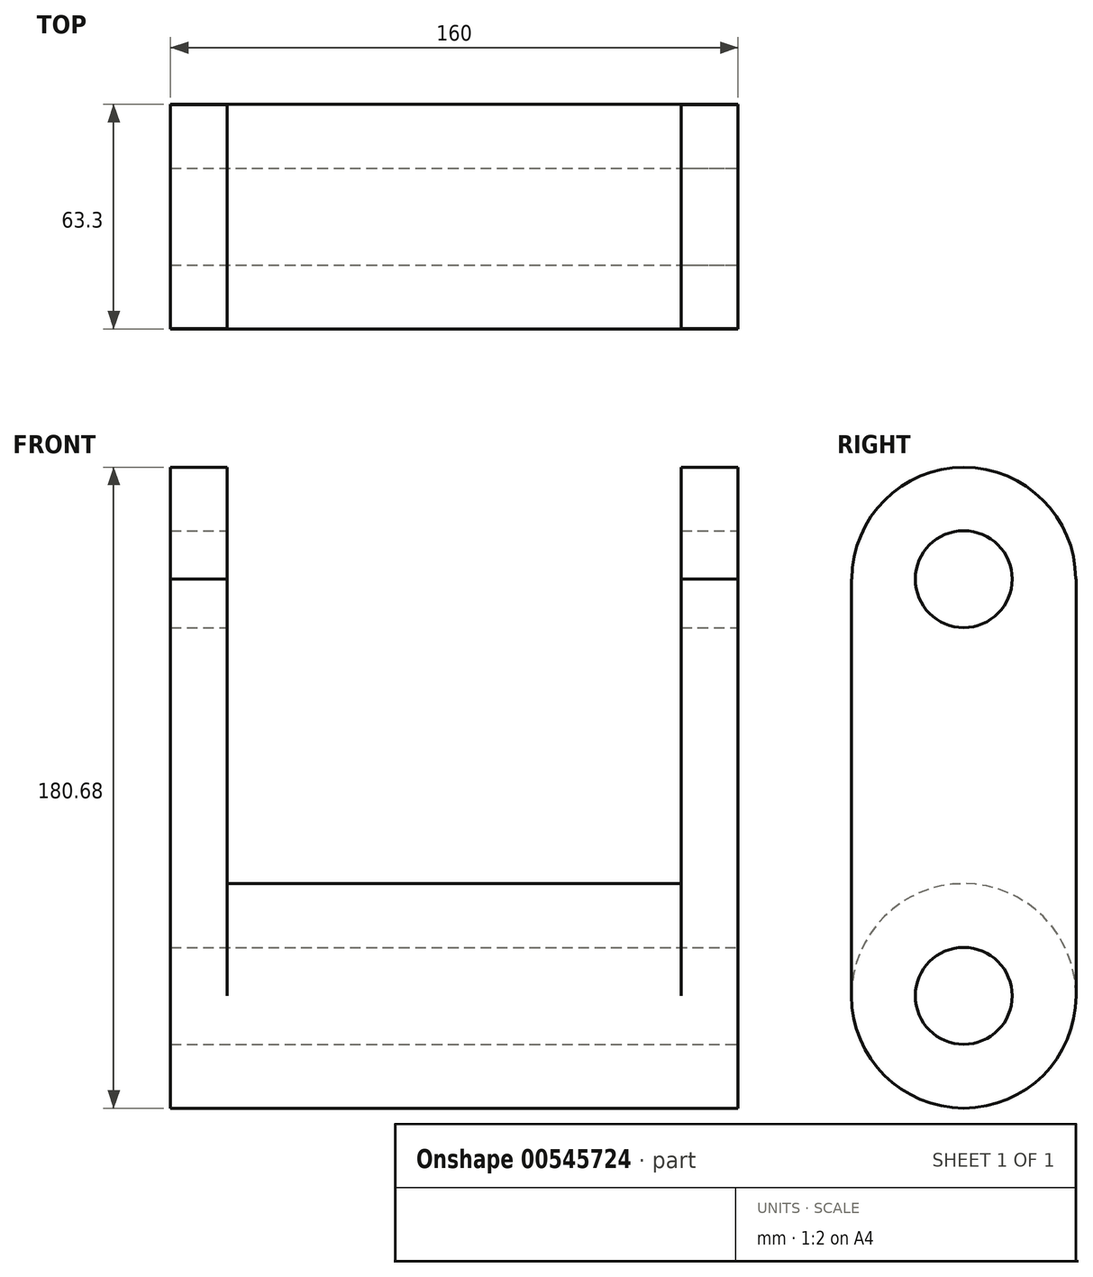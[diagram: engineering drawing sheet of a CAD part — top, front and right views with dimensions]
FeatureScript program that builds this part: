
annotation { "Feature Type Name" : "Feature", "Feature Type Description" : "" }
export const myFeature = defineFeature(function(context is Context, id is Id, definition is map)
    precondition{}
    {
        {
            var Q0;
            Q0=qCreatedBy(makeId("Right.planeOp"),FACE);
            var sketch = newSketch(context, id + "F0", { "sketchPlane" : qUnion([Q0])});
            skCircle(sketch, "E0", {"center": v(0, 0) * mm, "radius": 31.65 * mm});
            skSolve(sketch);
        }
        {
            var Q0;
            Q0 = qSketchRegion(id + "F0", true);
            extrude(context, id + "F1", {"entities" : qUnion([Q0]), "depth" : 80 * mm, "offsetDistance" : 25 * mm});
        }
        {
            var Q0;
            Q0=makeQuery(id+"F1.opExtrude","CAP_FACE",FACE,{"disambiguationData":[OSD([sQuery(id+"F0.wireOp",EDGE,"E0")])],"isStart":false});
            var sketch = newSketch(context, id + "F2", { "sketchPlane" : qUnion([Q0])});
            skPoint(sketch, "E1.end.orphan", {"position": v(-31.65, 117.5) * mm});
            skPoint(sketch, "E1.start.orphan", {"position": v(-31.65, 0) * mm});
            skPoint(sketch, "E2.end.orphan", {"position": v(31.65, 117.5) * mm});
            skPoint(sketch, "E2.start.orphan", {"position": v(31.65, 0) * mm});
            skLineSegment(sketch, "E3.bottom", {"start": v(31.65, 117.5) * mm, "end": v(-31.65, 117.5) * mm});
            skLineSegment(sketch, "E3.left", {"start": v(31.65, 117.5) * mm, "end": v(31.65, 0) * mm});
            skLineSegment(sketch, "E3.right", {"start": v(-31.65, 117.5) * mm, "end": v(-31.65, 0) * mm});
            skPoint(sketch, "E3.middle", {"position": v(0, 0) * mm});
            skPoint(sketch, "E4.middle", {"position": v(-39.72, -36.46) * mm});
            skPoint(sketch, "E4.top.end.orphan", {"position": v(-47.8, -32.34) * mm});
            skPoint(sketch, "E4.bottom.end.orphan", {"position": v(-47.8, -40.58) * mm});
            skPoint(sketch, "E5.trimOffspring.start.orphan", {"position": v(-31.65, -40.58) * mm});
            skPoint(sketch, "E6.orphan", {"position": v(-31.65, -32.34) * mm});
            skPoint(sketch, "E3.top.end.orphan", {"position": v(-31.65, -117.5) * mm});
            skPoint(sketch, "E3.top.start.orphan", {"position": v(31.65, -117.5) * mm});
            skLineSegment(sketch, "E7", {"start": v(-31.65, 0) * mm, "end": v(31.65, 0) * mm});
            skArc(sketch, "E8", {"start": v(31.65, 0) * mm, "mid": v(0, 31.65) * mm, "end": v(-31.65, 0) * mm});
            skArc(sketch, "E9", {"start": v(-31.65, 0) * mm, "mid": v(0, -31.65) * mm, "end": v(31.65, 0) * mm});
            skSolve(sketch);
        }
        {
            var Q0;
            Q0 = qSketchRegion(id + "F2", true);
            extrude(context, id + "F3", {"entities" : qUnion([Q0]), "operationType" : NewBodyOperationType.ADD, "oppositeDirection" : true, "depth" : 16 * mm, "offsetDistance" : 25 * mm});
        }
        {
            var Q0;
            Q0=makeQuery(id+"F3.boolean.opBoolean","MERGE",FACE,{"derivedFrom":[makeQuery(id+"F1.opExtrude","CAP_FACE",FACE,{"disambiguationData":[OSD([sQuery(id+"F0.wireOp",EDGE,"E0")])],"isStart":false}),makeQuery(id+"F3.opExtrude","CAP_FACE",FACE,{"disambiguationData":[OSD([sQuery(id+"F2.wireOp",EDGE,"E3.bottom"),sQuery(id+"F2.wireOp",EDGE,"E3.left"),sQuery(id+"F2.wireOp",EDGE,"E3.right"),sQuery(id+"F2.wireOp",EDGE,"E9")])],"isStart":true})]});
            var sketch = newSketch(context, id + "F4", { "sketchPlane" : qUnion([Q0])});
            skCircle(sketch, "E10", {"center": v(0, 117.5) * mm, "radius": 31.53 * mm});
            skSolve(sketch);
        }
        {
            var Q0;
            Q0 = qSketchRegion(id + "F4", true);
            extrude(context, id + "F5", {"entities" : qUnion([Q0]), "operationType" : NewBodyOperationType.ADD, "oppositeDirection" : true, "depth" : 16 * mm, "offsetDistance" : 25 * mm});
        }
        {
            var Q0;
            Q0=makeQuery(id+"F1.opExtrude","SWEPT_BODY",BODY,{"disambiguationData":[OSD([sQuery(id+"F0.wireOp",EDGE,"E0")])]});
            var Q1;
            Q1=makeQuery(id+"F1.opExtrude","CAP_FACE",FACE,{"disambiguationData":[OSD([sQuery(id+"F0.wireOp",EDGE,"E0")])],"isStart":true});
            mirror(context, id + "F6", {"operationType" : NewBodyOperationType.ADD, "entities" : qUnion([Q0]), "mirrorPlane" : qUnion([Q1])});
        }
        {
            var Q0;
            Q0=makeQuery(id+"F5.boolean.opBoolean","MERGE",FACE,{"derivedFrom":[makeQuery(id+"F3.boolean.opBoolean","MERGE",FACE,{"derivedFrom":[makeQuery(id+"F1.opExtrude","CAP_FACE",FACE,{"disambiguationData":[OSD([sQuery(id+"F0.wireOp",EDGE,"E0")])],"isStart":false}),makeQuery(id+"F3.opExtrude","CAP_FACE",FACE,{"disambiguationData":[OSD([sQuery(id+"F2.wireOp",EDGE,"E3.bottom"),sQuery(id+"F2.wireOp",EDGE,"E3.left"),sQuery(id+"F2.wireOp",EDGE,"E3.right"),sQuery(id+"F2.wireOp",EDGE,"E9")])],"isStart":true})]}),makeQuery(id+"F5.opExtrude","CAP_FACE",FACE,{"disambiguationData":[OSD([sQuery(id+"F4.wireOp",EDGE,"E10")])],"isStart":true})]});
            var sketch = newSketch(context, id + "F7", { "sketchPlane" : qUnion([Q0])});
            skCircle(sketch, "E11", {"center": v(0, 0) * mm, "radius": 13.66 * mm});
            skSolve(sketch);
        }
        {
            var Q0;
            Q0 = qSketchRegion(id + "F7", true);
            extrude(context, id + "F8", {"entities" : qUnion([Q0]), "operationType" : NewBodyOperationType.REMOVE, "oppositeDirection" : true, "depth" : 193 * mm, "offsetDistance" : 25 * mm});
        }
        {
            var Q0;
            Q0=makeQuery(id+"F5.boolean.opBoolean","MERGE",FACE,{"derivedFrom":[makeQuery(id+"F3.boolean.opBoolean","MERGE",FACE,{"derivedFrom":[makeQuery(id+"F1.opExtrude","CAP_FACE",FACE,{"disambiguationData":[OSD([sQuery(id+"F0.wireOp",EDGE,"E0")])],"isStart":false}),makeQuery(id+"F3.opExtrude","CAP_FACE",FACE,{"disambiguationData":[OSD([sQuery(id+"F2.wireOp",EDGE,"E3.bottom"),sQuery(id+"F2.wireOp",EDGE,"E3.left"),sQuery(id+"F2.wireOp",EDGE,"E3.right"),sQuery(id+"F2.wireOp",EDGE,"E9")])],"isStart":true})]}),makeQuery(id+"F5.opExtrude","CAP_FACE",FACE,{"disambiguationData":[OSD([sQuery(id+"F4.wireOp",EDGE,"E10")])],"isStart":true})]});
            var sketch = newSketch(context, id + "F9", { "sketchPlane" : qUnion([Q0])});
            skCircle(sketch, "E12", {"center": v(0, 117.5) * mm, "radius": 13.66 * mm});
            skSolve(sketch);
        }
        {
            var Q0;
            Q0 = qSketchRegion(id + "F9", true);
            extrude(context, id + "F10", {"entities" : qUnion([Q0]), "operationType" : NewBodyOperationType.REMOVE, "oppositeDirection" : true, "depth" : 212 * mm, "offsetDistance" : 25 * mm});
        }
    });
